SOLIDWORKS PART (.sldprt)
format: sldprt  version: not decoded by parser v0  size: 144,896 bytes
history: native  units: mm
features: plane x4, sketch x4, revolve x2, material x1, fillet x1, sweep x1, mirror x1 (+9 scaffold rows collapsed)
feature tree (23):
  scaffold x9  (default folders/planes/origin — collapsed)
  material  "Matériau <non spécifié>"
  plane  "Face"
  plane  "Dessus"
  plane  "Droite"
  sketch  "Esquisse1"  dims[D1=0.8mm]
  revolve  "Base-Révolution"  Angle=360deg
  sketch  "Esquisse2"  dims[c1.D1=1.0mm c1.D2=1.0mm c2.D1=0.25mm c2.D2=0.25mm]
  revolve  "Boss.-Révol.1"  Angle=360deg
  fillet  "Congé1"  Radius=0.05mm
  sketch  "Esquisse3"  dims[D1=~0.230252mm]
  sketch  "Esquisse4"  dims[D3=1.0mm D1=3.0mm D2=5.5mm]
  sweep  "Balayage1"
  plane  "Plan1"
  mirror  "Symétrie1"
decode coverage: 7 of 9 modeling features carry decoded parameters
note: ~ marks probable driven/reference dimensions
note: suppression state not decoded; provenance and decode notes live in map.json
